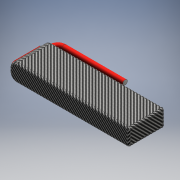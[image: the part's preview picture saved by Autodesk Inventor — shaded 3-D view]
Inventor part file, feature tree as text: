
AUTODESK INVENTOR PART (.ipt)
format: ipt  version: 2016 (Build 200138000, 138)  size: 256,000 bytes
history: native  units: mm
features: sketch x5, sweep x2, fillet x2, projected_geometry x2, extrude x1, plane x1
ambient origin geometry x8: Origin, YZ Plane, XZ Plane, XY Plane, X Axis, Y Axis, Z Axis, Center Point
bodies: Solid1 (feature_tree)
feature tree (13):
  extrude  "Extrusion1"  Depth=42.0mm
  sweep  "Sweep1"
  fillet  "Fillet1"  Radius=5.5mm
  plane  "Work Plane1"
  sweep  "Sweep2"
  fillet  "Fillet2"  Radius=8.0mm
  sketch  "Sketch1"  dims[d0=140.0mm d1=42.0mm]
  sketch  "Sketch2"  dims[d2=20.0mm d3=0.0mm d4=5.5mm d5=5.5mm]
  projected_geometry  "Projected Loop1"
  sketch  "Sketch3"  dims[d6=7.0mm d7=0.0mm d8=0.0mm d9=8.0mm]
  sketch  "Sketch4"  dims[d10=1.5mm]
  projected_geometry  "Projected Loop2"
  sketch  "Sketch5"  dims[d11=1.5mm d12=0.75mm d13=1.5mm d14=0.0mm d15=0.0mm d16=2.0mm]
